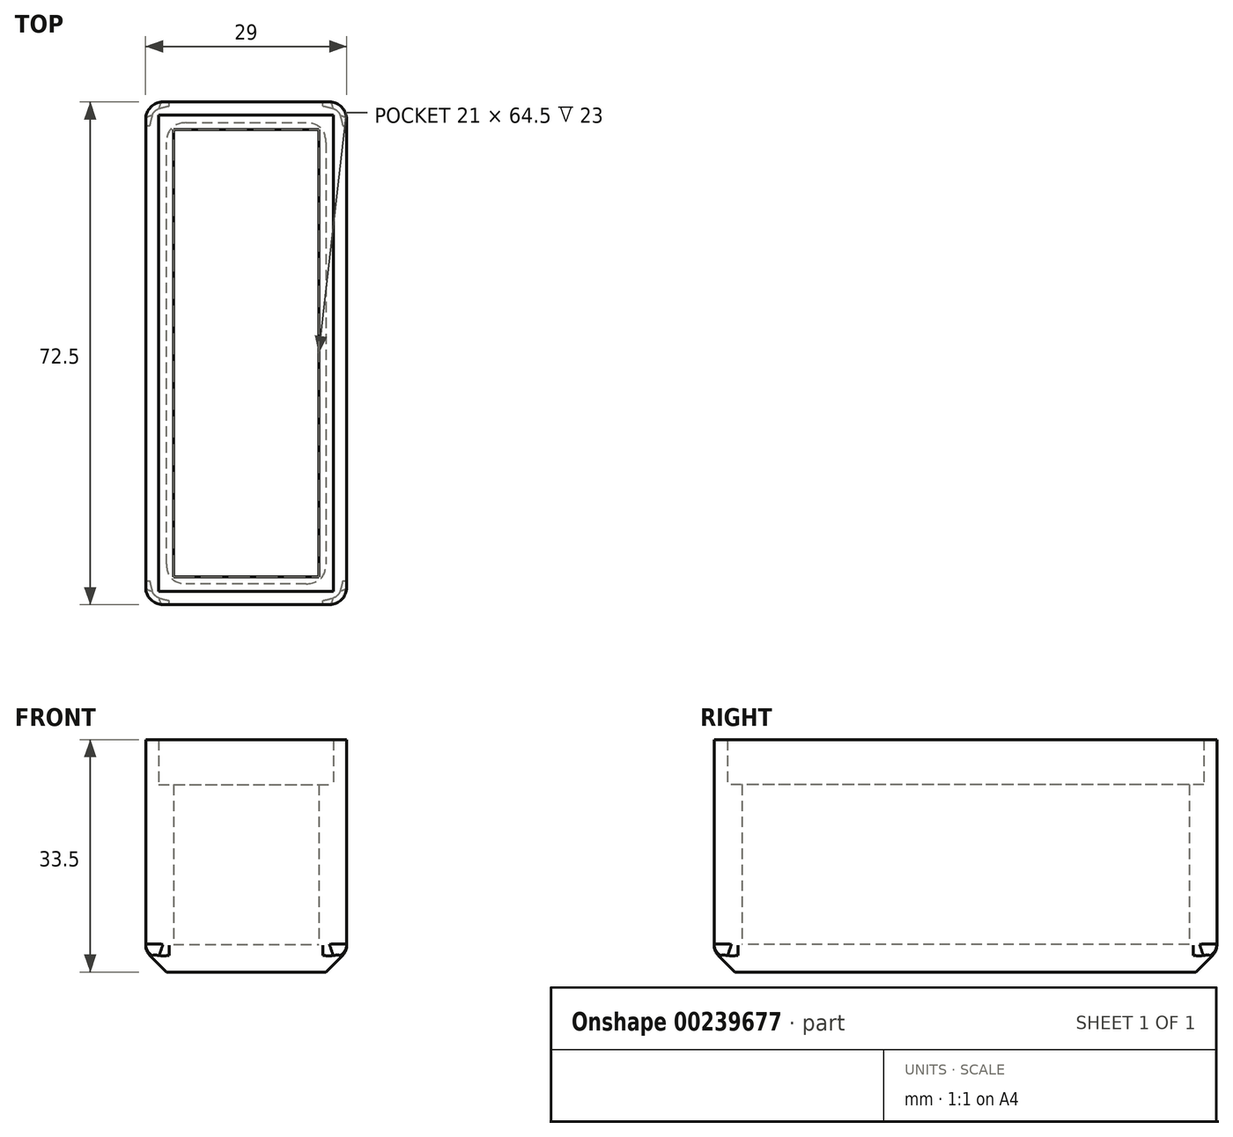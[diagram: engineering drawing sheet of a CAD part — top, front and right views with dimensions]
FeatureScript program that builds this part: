
annotation { "Feature Type Name" : "Feature", "Feature Type Description" : "" }
export const myFeature = defineFeature(function(context is Context, id is Id, definition is map)
    precondition{}
    {
        {
            var Q0;
            Q0=qCreatedBy(makeId("Top.planeOp"),FACE);
            var sketch = newSketch(context, id + "F0", { "sketchPlane" : qUnion([Q0])});
            skLineSegment(sketch, "E0.bottom", {"start": v(-9.85, 54.93) * mm, "end": v(11.15, 54.93) * mm});
            skLineSegment(sketch, "E0.top", {"start": v(-9.85, -9.57) * mm, "end": v(11.15, -9.57) * mm});
            skLineSegment(sketch, "E0.left", {"start": v(-9.85, 54.93) * mm, "end": v(-9.85, -9.57) * mm});
            skLineSegment(sketch, "E0.right", {"start": v(11.15, 54.93) * mm, "end": v(11.15, -9.57) * mm});
            skLineSegment(sketch, "E1.0", {"start": v(-13.85, 58.93) * mm, "end": v(15.15, 58.93) * mm});
            skLineSegment(sketch, "E1.1", {"start": v(-13.85, 58.93) * mm, "end": v(-13.85, -13.57) * mm});
            skLineSegment(sketch, "E1.2", {"start": v(-13.85, -13.57) * mm, "end": v(15.15, -13.57) * mm});
            skLineSegment(sketch, "E1.3", {"start": v(15.15, 58.93) * mm, "end": v(15.15, -13.57) * mm});
            skLineSegment(sketch, "E2.0", {"start": v(-11.95, 57.03) * mm, "end": v(13.25, 57.03) * mm});
            skLineSegment(sketch, "E2.1", {"start": v(-11.95, 57.03) * mm, "end": v(-11.95, -11.67) * mm});
            skLineSegment(sketch, "E2.2", {"start": v(-11.95, -11.67) * mm, "end": v(13.25, -11.67) * mm});
            skLineSegment(sketch, "E2.3", {"start": v(13.25, 57.03) * mm, "end": v(13.25, -11.67) * mm});
            skSolve(sketch);
        }
        {
            var Q0;
            Q0=makeQuery(id+"F0.imprint","IMPRINT",FACE,{"disambiguationData":[TD([[makeQuery(id+"F0.imprint","IMPRINT",EDGE,{"derivedFrom":sQuery(id+"F0.wireOp",EDGE,"E1.0")}),-1.0]])]});
            extrude(context, id + "F1", {"entities" : qUnion([Q0]), "depth" : 33.5 * mm});
        }
        {
            var Q0;
            Q0=makeQuery(id+"F0.imprint","IMPRINT",FACE,{"disambiguationData":[TD([[makeQuery(id+"F0.imprint","IMPRINT",EDGE,{"derivedFrom":sQuery(id+"F0.wireOp",EDGE,"E0.bottom")}),1.0]])]});
            extrude(context, id + "F2", {"entities" : qUnion([Q0]), "operationType" : NewBodyOperationType.ADD, "depth" : 27 * mm});
        }
        {
            var Q0;
            Q0=makeQuery(id+"F0.imprint","IMPRINT",FACE,{"disambiguationData":[TD([[makeQuery(id+"F0.imprint","IMPRINT",EDGE,{"derivedFrom":sQuery(id+"F0.wireOp",EDGE,"E0.bottom")}),-1.0]])]});
            extrude(context, id + "F3", {"entities" : qUnion([Q0]), "operationType" : NewBodyOperationType.ADD, "depth" : 4 * mm});
        }
        {
            var Q0;
            Q0=makeQuery(id+"F1.opExtrude","CAP_EDGE",EDGE,{"disambiguationData":[OSD([sQuery(id+"F0.wireOp",EDGE,"E1.1")])],"isStart":true});
            var Q1;
            Q1=makeQuery(id+"F1.opExtrude","CAP_EDGE",EDGE,{"disambiguationData":[OSD([sQuery(id+"F0.wireOp",EDGE,"E1.0")])],"isStart":true});
            var Q2;
            Q2=makeQuery(id+"F1.opExtrude","CAP_EDGE",EDGE,{"disambiguationData":[OSD([sQuery(id+"F0.wireOp",EDGE,"E1.3")])],"isStart":true});
            var Q3;
            Q3=makeQuery(id+"F1.opExtrude","CAP_EDGE",EDGE,{"disambiguationData":[OSD([sQuery(id+"F0.wireOp",EDGE,"E1.2")])],"isStart":true});
            chamfer(context, id + "F4", {"entities" : qUnion([Q0, Q1, Q2, Q3]), "width" : 3 * mm, "tangentPropagation" : true});
        }
        {
            var Q0;
            Q0=makeQuery(id+"F4.opChamfer","BLEND_EDGE",EDGE,{"blendedFrom":[makeQuery(id+"F1.opExtrude","CAP_EDGE",EDGE,{"disambiguationData":[OSD([sQuery(id+"F0.wireOp",EDGE,"E1.0")])],"isStart":true}),makeQuery(id+"F1.opExtrude","CAP_EDGE",EDGE,{"disambiguationData":[OSD([sQuery(id+"F0.wireOp",EDGE,"E1.3")])],"isStart":true})],"blendedInto":[]});
            var Q1;
            Q1=makeQuery(id+"F4.opChamfer","BLEND_EDGE",EDGE,{"blendedFrom":[makeQuery(id+"F1.opExtrude","CAP_EDGE",EDGE,{"disambiguationData":[OSD([sQuery(id+"F0.wireOp",EDGE,"E1.0")])],"isStart":true}),makeQuery(id+"F1.opExtrude","CAP_EDGE",EDGE,{"disambiguationData":[OSD([sQuery(id+"F0.wireOp",EDGE,"E1.1")])],"isStart":true})],"blendedInto":[]});
            var Q2;
            Q2=makeQuery(id+"F4.opChamfer","BLEND_EDGE",EDGE,{"blendedFrom":[makeQuery(id+"F1.opExtrude","CAP_EDGE",EDGE,{"disambiguationData":[OSD([sQuery(id+"F0.wireOp",EDGE,"E1.1")])],"isStart":true}),makeQuery(id+"F1.opExtrude","CAP_EDGE",EDGE,{"disambiguationData":[OSD([sQuery(id+"F0.wireOp",EDGE,"E1.2")])],"isStart":true})],"blendedInto":[]});
            var Q3;
            Q3=makeQuery(id+"F4.opChamfer","BLEND_EDGE",EDGE,{"blendedFrom":[makeQuery(id+"F1.opExtrude","CAP_EDGE",EDGE,{"disambiguationData":[OSD([sQuery(id+"F0.wireOp",EDGE,"E1.2")])],"isStart":true}),makeQuery(id+"F1.opExtrude","CAP_EDGE",EDGE,{"disambiguationData":[OSD([sQuery(id+"F0.wireOp",EDGE,"E1.3")])],"isStart":true})],"blendedInto":[]});
            fillet(context, id + "F5", {"entities" : qUnion([Q0, Q1, Q2, Q3]), "radius" : 4 * mm, "tangentPropagation" : true, "allowEdgeOverflow" : false});
        }
        {
            var Q0;
            Q0=makeQuery(id+"F1.opExtrude","SWEPT_EDGE",EDGE,{"disambiguationData":[OSD([sQuery(id+"F0.wireOp",EDGE,"E1.1"),sQuery(id+"F0.wireOp",EDGE,"E1.2")])]});
            var Q1;
            Q1=makeQuery(id+"F1.opExtrude","SWEPT_EDGE",EDGE,{"disambiguationData":[OSD([sQuery(id+"F0.wireOp",EDGE,"E1.2"),sQuery(id+"F0.wireOp",EDGE,"E1.3")])]});
            var Q2;
            Q2=makeQuery(id+"F1.opExtrude","SWEPT_EDGE",EDGE,{"disambiguationData":[OSD([sQuery(id+"F0.wireOp",EDGE,"E1.0"),sQuery(id+"F0.wireOp",EDGE,"E1.3")])]});
            var Q3;
            Q3=makeQuery(id+"F1.opExtrude","SWEPT_EDGE",EDGE,{"disambiguationData":[OSD([sQuery(id+"F0.wireOp",EDGE,"E1.0"),sQuery(id+"F0.wireOp",EDGE,"E1.1")])]});
            fillet(context, id + "F6", {"entities" : qUnion([Q0, Q1, Q2, Q3]), "radius" : 2.5 * mm, "tangentPropagation" : true, "allowEdgeOverflow" : false});
        }
        {
            var Q0;
            {var subQ0=sQuery(id+"F0.wireOp",EDGE,"E1.3");Q0=makeQuery(id+"F4.opChamfer","BLEND_EDGE",EDGE,{"blendedFrom":[makeQuery(id+"F1.opExtrude","CAP_EDGE",EDGE,{"disambiguationData":[OSD([subQ0])],"isStart":true}),makeQuery(id+"F1.opExtrude","SWEPT_FACE",FACE,{"disambiguationData":[OSD([subQ0])]})],"blendedInto":[makeQuery(id+"F1.opExtrude","SWEPT_FACE",FACE,{"disambiguationData":[OSD([subQ0])]})]});}
            fillet(context, id + "F7", {"entities" : qUnion([Q0]), "radius" : 2 * mm, "tangentPropagation" : true, "allowEdgeOverflow" : false});
        }
    });
